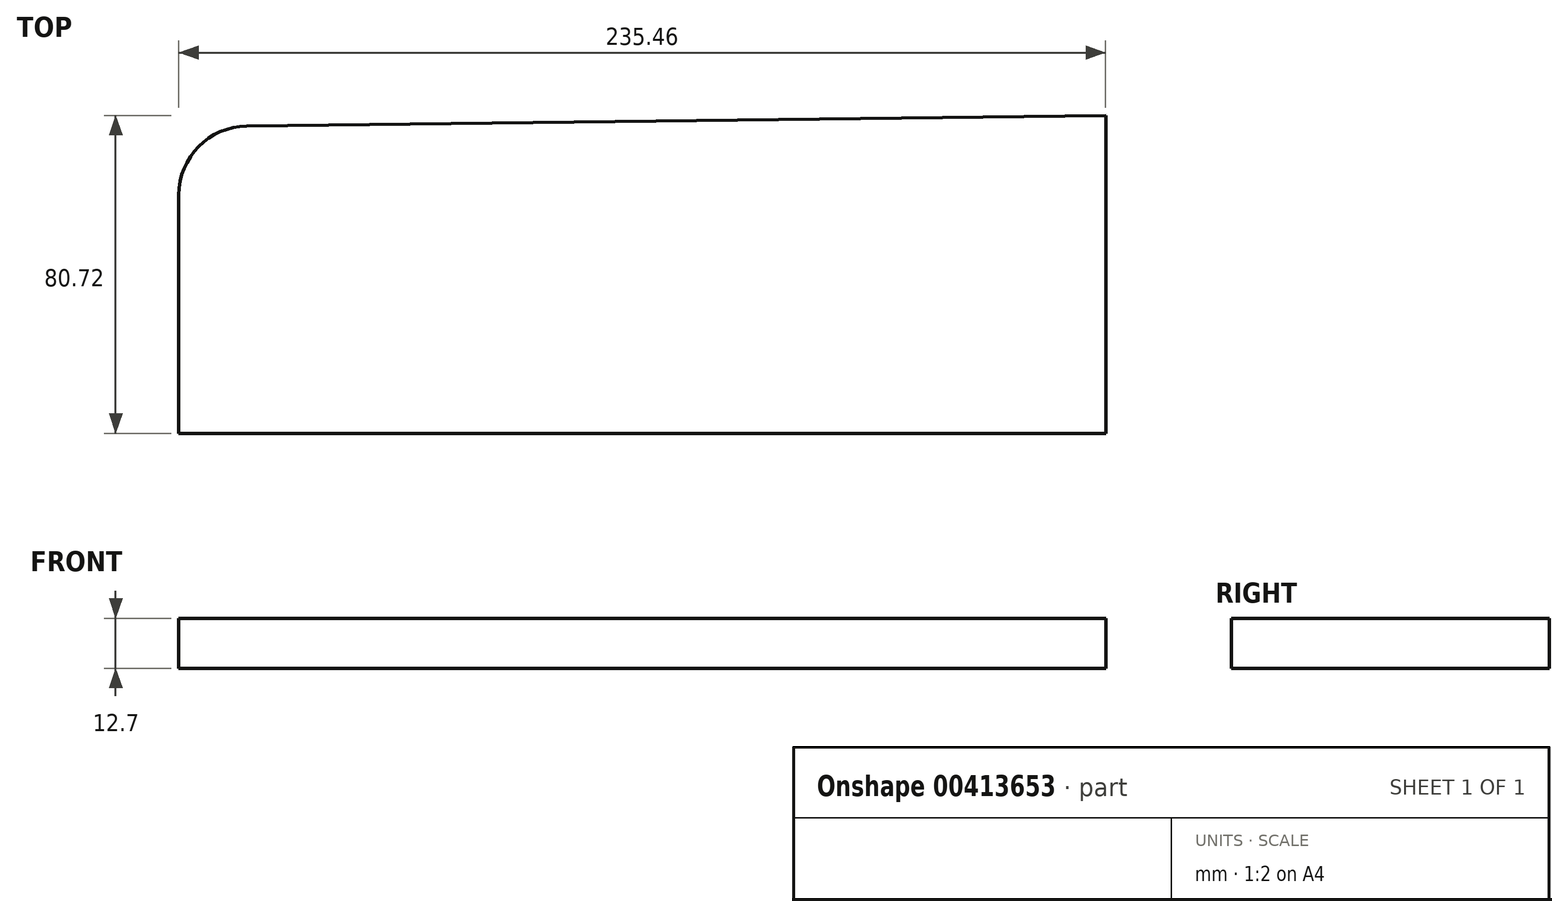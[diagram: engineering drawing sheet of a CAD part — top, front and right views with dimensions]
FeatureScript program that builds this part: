
annotation { "Feature Type Name" : "Feature", "Feature Type Description" : "" }
export const myFeature = defineFeature(function(context is Context, id is Id, definition is map)
    precondition{}
    {
        {
            var Q0;
            Q0=qCreatedBy(makeId("Top.planeOp"),FACE);
            var sketch = newSketch(context, id + "F0", { "sketchPlane" : qUnion([Q0])});
            skLineSegment(sketch, "E0.top", {"start": v(117.74, -38.92) * mm, "end": v(-117.74, -38.92) * mm});
            skLineSegment(sketch, "E0.left", {"start": v(117.74, 38.92) * mm, "end": v(117.74, -38.92) * mm});
            skLineSegment(sketch, "E0.right", {"start": v(-117.74, 21.65) * mm, "end": v(-117.74, -38.92) * mm});
            skPoint(sketch, "E0.middle", {"position": v(0, 0) * mm});
            skLineSegment(sketch, "E1", {"start": v(-100.47, 39.13) * mm, "end": v(117.74, 41.8) * mm});
            skLineSegment(sketch, "E2", {"start": v(117.74, 41.8) * mm, "end": v(117.74, 38.92) * mm});
            skPoint(sketch, "E3.visualSharp", {"position": v(-117.73, 38.92) * mm});
            skArc(sketch, "E3.filletArc", {"start": v(-100.47, 39.13) * mm, "mid": v(-112.7, 33.94) * mm, "end": v(-117.74, 21.65) * mm});
            skSolve(sketch);
        }
        {
            var Q0;
            Q0=makeQuery(id+"F0.imprint","IMPRINT",FACE,{"disambiguationData":[TD([[makeQuery(id+"F0.imprint","IMPRINT",EDGE,{"derivedFrom":sQuery(id+"F0.wireOp",EDGE,"E0.top")}),-1.0]])]});
            extrude(context, id + "F1", {"entities" : qUnion([Q0]), "depth" : 12.7 * mm});
        }
    });
